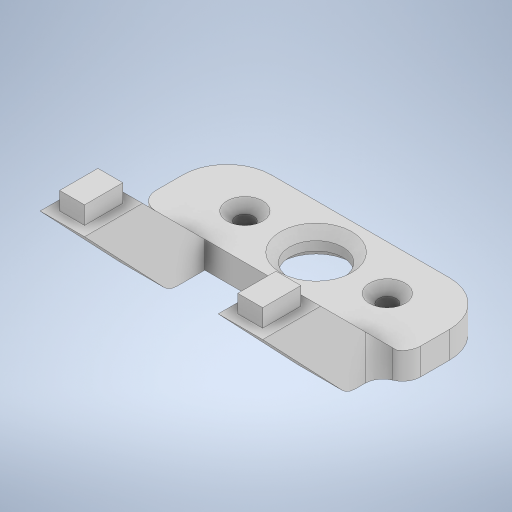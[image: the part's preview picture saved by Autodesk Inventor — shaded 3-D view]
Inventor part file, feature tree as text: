
AUTODESK INVENTOR PART (.ipt)
format: ipt  version: 2024.2 (Build 282272000, 272)  size: 343,040 bytes
history: native  units: mm
features: extrude x5, sketch x5, fillet x4, chamfer x3, plane x2, mirror x1
ambient origin geometry x8: Origin, YZ Plane, XZ Plane, XY Plane, X Axis, Y Axis, Z Axis, Center Point
bodies: Solid1 (feature_tree)
feature tree (20):
  extrude  "Extrusion1"  Depth=10.0mm
  plane  "Work Plane2"
  extrude  "Extrusion3"  [1 undecoded]
  plane  "Work Plane3"
  fillet  "Fillet2"  Radius=4.0mm
  fillet  "Fillet3"  Radius=6.5mm
  fillet  "Fillet4"  [1 undecoded]
  extrude  "Extrusion4"  Depth=5.0mm TaperAngle=0.0deg
  mirror  "Mirror2"
  extrude  "Extrusion5"  Depth=2.0mm
  chamfer  "Chamfer1"  Distance=2.8mm
  extrude  "Extrusion6"  Depth=4.3mm
  chamfer  "Chamfer2"  Distance=1.1mm
  fillet  "Fillet5"  Radius=1.1mm
  chamfer  "Chamfer3"  Distance=2.0mm
  sketch  "Sketch1"  dims[d0=30.0mm d1=10.0mm]
  sketch  "Sketch3"  dims[d2=3.0mm d3=0.0mm d12=-2.5mm d13=4.0mm d14=6.5mm d15=45.0deg]
  sketch  "Sketch5"  dims[d16=10.0mm d17=5.0mm d18=0.0mm]
  sketch  "Sketch6"  dims[d19=-15.0mm d20=2.0mm d21=2.0mm]
  sketch  "Sketch7"  dims[d22=5.0mm d26=2.8mm d27=4.3mm d28=1.1mm d29=1.1mm d30=2.0mm d31=0.0mm d32=6.0mm d33=5.0mm d34=15.0mm d35=0.0mm d36=0.0mm d37=1.0mm d38=2.0mm d39=45.0deg d40=2.0mm d41=2.0mm d42=5.0mm d43=5.0mm d44=8.0mm d45=8.0mm d46=0.0mm d47=0.0mm d48=1.0mm d49=2.0mm d50=45.0deg d51=2.0mm d52=1.0mm d53=2.0mm d54=45.0deg]
note: 2 required parameter values undecoded (feature->parameter linkage not recoverable at this tier; creation-order binding heuristic only, values carry confidence <= 0.55)
